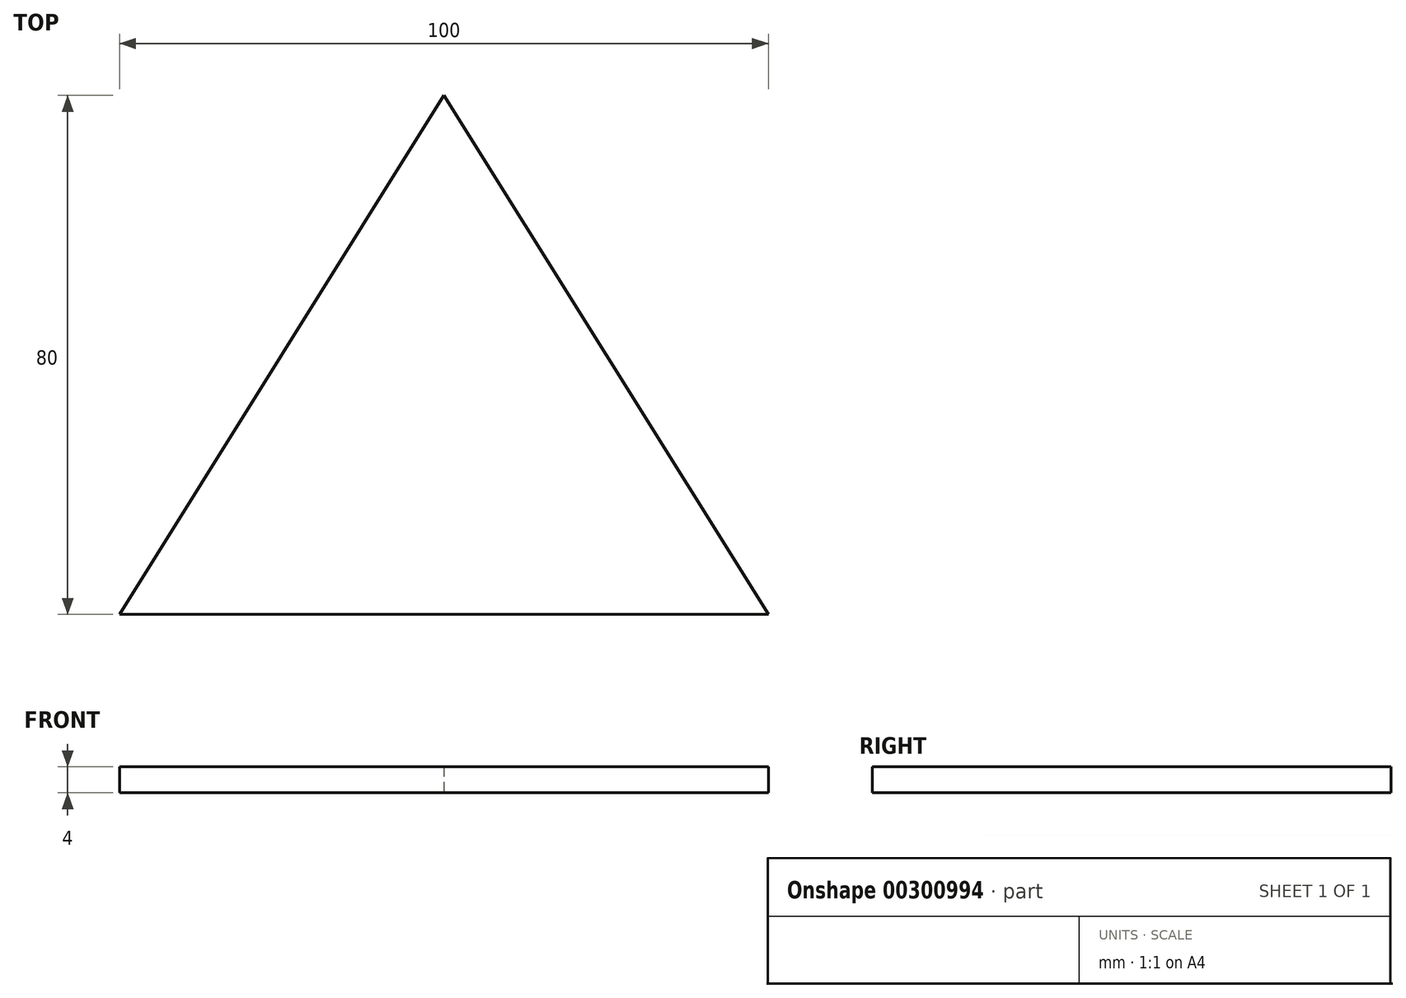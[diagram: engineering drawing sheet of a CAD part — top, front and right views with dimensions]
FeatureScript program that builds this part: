
annotation { "Feature Type Name" : "Feature", "Feature Type Description" : "" }
export const myFeature = defineFeature(function(context is Context, id is Id, definition is map)
    precondition{}
    {
        {
            var Q0;
            Q0=qCreatedBy(makeId("Top.planeOp"),FACE);
            var sketch = newSketch(context, id + "F0", { "sketchPlane" : qUnion([Q0])});
            skLineSegment(sketch, "E0", {"start": v(0, 0) * mm, "end": v(0, 80) * mm});
            skLineSegment(sketch, "E1", {"start": v(0, 0) * mm, "end": v(-50, 0) * mm});
            skLineSegment(sketch, "E2", {"start": v(0, 0) * mm, "end": v(50, 0) * mm});
            skLineSegment(sketch, "E3", {"start": v(-50, 0) * mm, "end": v(0, 80) * mm});
            skLineSegment(sketch, "E4", {"start": v(0, 80) * mm, "end": v(50, 0) * mm});
            skSolve(sketch);
        }
        {
            var Q0;
            Q0=makeQuery(id+"F0.imprint","IMPRINT",FACE,{"disambiguationData":[TD([[makeQuery(id+"F0.imprint","IMPRINT",EDGE,{"derivedFrom":sQuery(id+"F0.wireOp",EDGE,"E0")}),1.0]])]});
            var Q1;
            Q1=makeQuery(id+"F0.imprint","IMPRINT",FACE,{"disambiguationData":[TD([[makeQuery(id+"F0.imprint","IMPRINT",EDGE,{"derivedFrom":sQuery(id+"F0.wireOp",EDGE,"E0")}),-1.0]])]});
            extrude(context, id + "F1", {"entities" : qUnion([Q0, Q1]), "depth" : 4 * mm});
        }
    });
